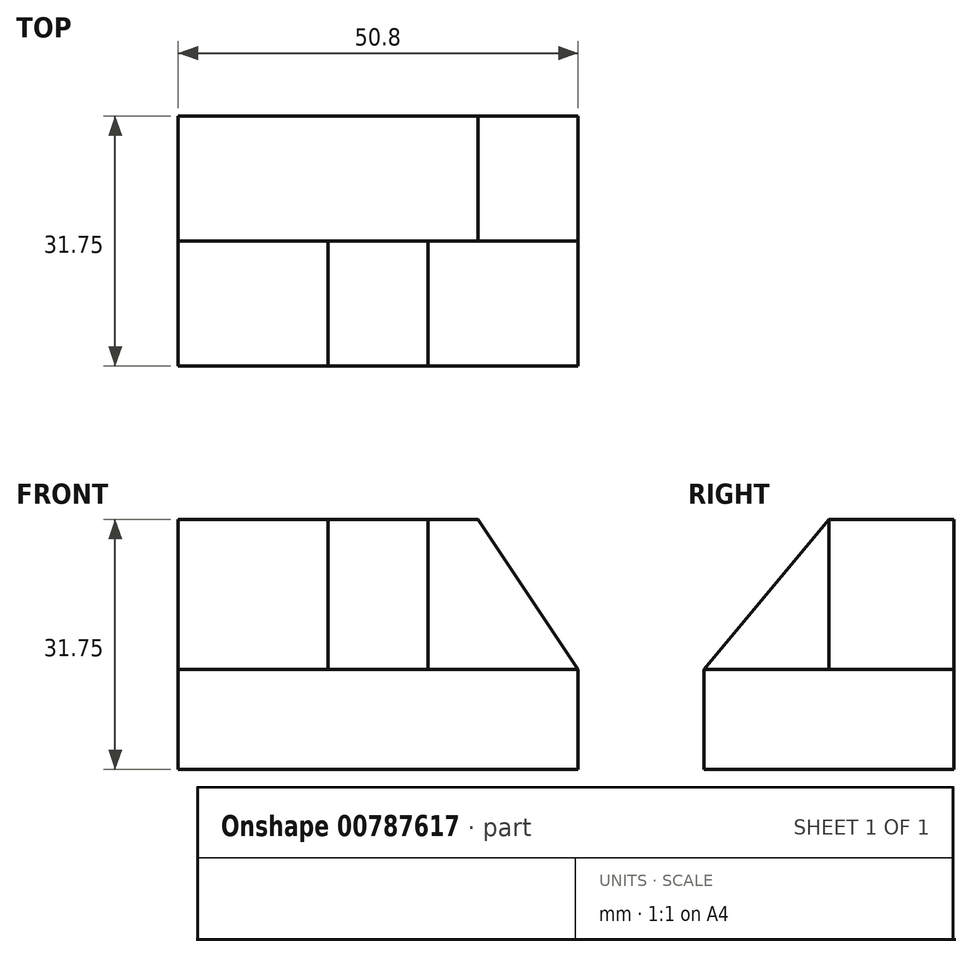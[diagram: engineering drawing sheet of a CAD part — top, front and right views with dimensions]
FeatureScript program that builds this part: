
annotation { "Feature Type Name" : "Feature", "Feature Type Description" : "" }
export const myFeature = defineFeature(function(context is Context, id is Id, definition is map)
    precondition{}
    {
        {
            var Q0;
            Q0=qCreatedBy(makeId("Front.planeOp"),FACE);
            var sketch = newSketch(context, id + "F0", { "sketchPlane" : qUnion([Q0])});
            skLineSegment(sketch, "E0", {"start": v(0, 0) * mm, "end": v(0, -12.7) * mm});
            skLineSegment(sketch, "E1", {"start": v(0, -12.7) * mm, "end": v(50.8, -12.7) * mm});
            skLineSegment(sketch, "E2", {"start": v(50.8, -12.7) * mm, "end": v(50.8, 0) * mm});
            skLineSegment(sketch, "E3", {"start": v(50.8, 0) * mm, "end": v(0, 0) * mm});
            skSolve(sketch);
        }
        {
            var Q0;
            Q0=makeQuery(id+"F0.imprint","IMPRINT",FACE,{"disambiguationData":[TD([[makeQuery(id+"F0.imprint","IMPRINT",EDGE,{"derivedFrom":sQuery(id+"F0.wireOp",EDGE,"E0")}),1.0]])]});
            extrude(context, id + "F1", {"entities" : qUnion([Q0]), "depth" : 31.75 * mm, "offsetDistance" : 25.4 * mm});
        }
        {
            var Q0;
            Q0=makeQuery(id+"F1.opExtrude","SWEPT_FACE",FACE,{"disambiguationData":[OSD([sQuery(id+"F0.wireOp",EDGE,"E3")])]});
            var sketch = newSketch(context, id + "F2", { "sketchPlane" : qUnion([Q0])});
            skLineSegment(sketch, "E4", {"start": v(0, 0) * mm, "end": v(0, -15.88) * mm});
            skLineSegment(sketch, "E5", {"start": v(0, -15.88) * mm, "end": v(50.8, -15.88) * mm});
            skSolve(sketch);
        }
        {
            var Q0;
            Q0=makeQuery(id+"F2.imprint","IMPRINT",FACE,{"disambiguationData":[TD([[makeQuery(id+"F2.imprint","IMPRINT",EDGE,{"derivedFrom":sQuery(id+"F2.wireOp",EDGE,"E4")}),-1.0]])]});
            extrude(context, id + "F3", {"entities" : qUnion([Q0]), "operationType" : NewBodyOperationType.ADD, "depth" : 19.05 * mm, "offsetDistance" : 25.4 * mm});
        }
        {
            var Q0;
            Q0=makeQuery(id+"F3.opExtrude","SWEPT_FACE",FACE,{"disambiguationData":[OSD([sQuery(id+"F2.wireOp",EDGE,"E5")])]});
            var sketch = newSketch(context, id + "F4", { "sketchPlane" : qUnion([Q0])});
            skLineSegment(sketch, "E6", {"start": v(50.8, 19.05) * mm, "end": v(38.1, 19.05) * mm});
            skLineSegment(sketch, "E7", {"start": v(38.1, 19.05) * mm, "end": v(50.8, 0) * mm});
            skSolve(sketch);
        }
        {
            var Q0;
            Q0=makeQuery(id+"F4.imprint","IMPRINT",FACE,{"disambiguationData":[TD([[makeQuery(id+"F4.imprint","IMPRINT",EDGE,{"derivedFrom":sQuery(id+"F4.wireOp",EDGE,"E6")}),-1.0]])]});
            extrude(context, id + "F5", {"entities" : qUnion([Q0]), "operationType" : NewBodyOperationType.REMOVE, "oppositeDirection" : true, "depth" : 25.4 * mm, "offsetDistance" : 25.4 * mm});
        }
        {
            var Q0;
            Q0=makeQuery(id+"F1.opExtrude","SWEPT_FACE",FACE,{"disambiguationData":[OSD([sQuery(id+"F0.wireOp",EDGE,"E3")])]});
            var sketch = newSketch(context, id + "F6", { "sketchPlane" : qUnion([Q0])});
            skLineSegment(sketch, "E8", {"start": v(50.8, -15.88) * mm, "end": v(31.75, -15.88) * mm, "construction": true});
            skLineSegment(sketch, "E9", {"start": v(31.75, -15.88) * mm, "end": v(31.75, -31.75) * mm});
            skLineSegment(sketch, "E10", {"start": v(31.75, -31.75) * mm, "end": v(19.05, -31.75) * mm});
            skLineSegment(sketch, "E11", {"start": v(19.05, -31.75) * mm, "end": v(19.05, -15.88) * mm});
            skSolve(sketch);
        }
        {
            var Q0;
            {var subQ0=sQuery(id+"F6.wireOp",EDGE,"E9");Q0=makeQuery(id+"F6.imprint","IMPRINT",FACE,{"disambiguationData":[TD([[makeQuery(id+"F6.imprint","IMPRINT",EDGE,{"derivedFrom":subQ0}),-1.0]])]});}
            extrude(context, id + "F7", {"entities" : qUnion([Q0]), "operationType" : NewBodyOperationType.ADD, "depth" : 19.05 * mm, "offsetDistance" : 25.4 * mm});
        }
        {
            var Q0;
            Q0=makeQuery(id+"F7.opExtrude","SWEPT_FACE",FACE,{"disambiguationData":[OSD([sQuery(id+"F6.wireOp",EDGE,"E9")])]});
            var sketch = newSketch(context, id + "F8", { "sketchPlane" : qUnion([Q0])});
            skLineSegment(sketch, "E12", {"start": v(-15.88, 19.05) * mm, "end": v(-31.75, 0) * mm});
            skSolve(sketch);
        }
        {
            var Q0;
            Q0=makeQuery(id+"F8.imprint","IMPRINT",FACE,{"disambiguationData":[TD([[makeQuery(id+"F8.imprint","IMPRINT",EDGE,{"derivedFrom":sQuery(id+"F8.wireOp",EDGE,"E12")}),-1.0]])]});
            extrude(context, id + "F9", {"entities" : qUnion([Q0]), "operationType" : NewBodyOperationType.REMOVE, "endBound" : BoundingType.THROUGH_ALL, "oppositeDirection" : true, "depth" : 25.4 * mm, "offsetDistance" : 25.4 * mm});
        }
    });
